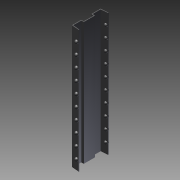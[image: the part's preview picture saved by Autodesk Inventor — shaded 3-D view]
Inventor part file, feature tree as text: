
AUTODESK INVENTOR PART (.ipt)
format: ipt  version: 2011 SP1 (Build 150282100, 282)  size: 129,536 bytes
history: native  units: mm
features: other x7, sketch x3, revolve x2, pattern_linear x2, extrude x1
ambient origin geometry x8: Origin, YZ Plane, XZ Plane, XY Plane, X Axis, Y Axis, Z Axis, Center Point
bodies: Solid1 (feature_tree)
feature tree (15):
  extrude  "Extrusion1"  TaperAngle=360.0deg  [1 undecoded]
  revolve  "Revolution1"  Angle=360.0deg
  pattern_linear  "Rectangular Pattern1"  Count1=10 Spacing1=11.7mm
  revolve  "Revolution2"  [1 undecoded]
  pattern_linear  "Rectangular Pattern2"  [2 undecoded]
  other  "to_rail_XY"
  other  "to_rail_YZ"
  other  "to_rail_ZX"
  other  "to_rail_X"
  other  "to_rail_Y"
  other  "to_rail_Z"
  other  "to_rail_Center"
  sketch  "Sketch_1"  dims[d0=127.0mm d1=0.0mm d2=360.0deg]
  sketch  "Sketch_2"  dims[d3=100.0mm d5=11.7mm d6=10.0mm d8=0.0mm d9=360.0deg d10=100.0mm d12=11.7mm d13=10.0mm d15=0.0mm]
  sketch  "Sketch_4"
note: 4 required parameter values undecoded (feature->parameter linkage not recoverable at this tier; creation-order binding heuristic only, values carry confidence <= 0.55)
